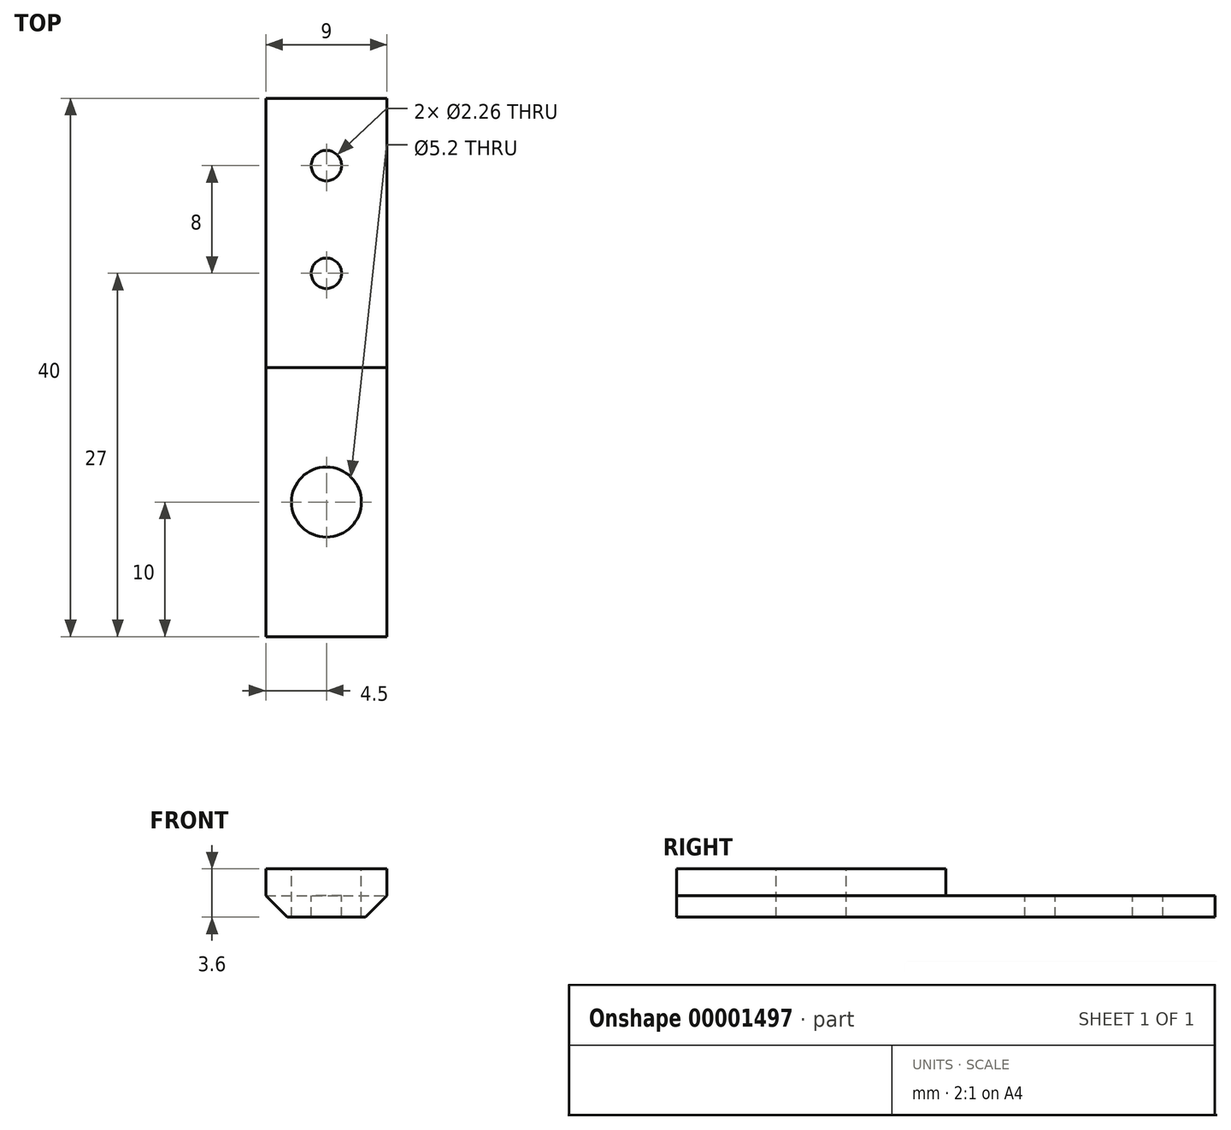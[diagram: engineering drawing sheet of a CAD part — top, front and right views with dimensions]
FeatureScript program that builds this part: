
annotation { "Feature Type Name" : "Feature", "Feature Type Description" : "" }
export const myFeature = defineFeature(function(context is Context, id is Id, definition is map)
    precondition{}
    {
        {
            var Q0;
            Q0=qCreatedBy(makeId("Front.planeOp"),FACE);
            var sketch = newSketch(context, id + "F0", { "sketchPlane" : qUnion([Q0])});
            skLineSegment(sketch, "E0", {"start": v(-4.5, 0) * mm, "end": v(4.5, 0) * mm});
            skLineSegment(sketch, "E1", {"start": v(4.5, 0) * mm, "end": v(2.9, -1.6) * mm});
            skLineSegment(sketch, "E2", {"start": v(2.9, -1.6) * mm, "end": v(-2.9, -1.6) * mm});
            skLineSegment(sketch, "E3", {"start": v(-2.9, -1.6) * mm, "end": v(-4.5, 0) * mm});
            skPoint(sketch, "E4", {"position": v(0, 0) * mm});
            skSolve(sketch);
        }
        {
            var Q0;
            Q0=makeQuery(id+"F0.imprint","IMPRINT",FACE,{"disambiguationData":[TD([[makeQuery(id+"F0.imprint","IMPRINT",EDGE,{"derivedFrom":sQuery(id+"F0.wireOp",EDGE,"E0")}),-1.0]])]});
            extrude(context, id + "F1", {"entities" : qUnion([Q0]), "depth" : 40 * mm});
        }
        {
            var Q0;
            Q0=makeQuery(id+"F1.opExtrude","SWEPT_FACE",FACE,{"disambiguationData":[OSD([sQuery(id+"F0.wireOp",EDGE,"E0")])]});
            var sketch = newSketch(context, id + "F2", { "sketchPlane" : qUnion([Q0])});
            skLineSegment(sketch, "E5.bottom", {"start": v(-4.5, -40) * mm, "end": v(4.5, -40) * mm});
            skLineSegment(sketch, "E5.top", {"start": v(-4.5, -20) * mm, "end": v(4.5, -20) * mm});
            skLineSegment(sketch, "E5.left", {"start": v(-4.5, -40) * mm, "end": v(-4.5, -20) * mm});
            skLineSegment(sketch, "E5.right", {"start": v(4.5, -40) * mm, "end": v(4.5, -20) * mm});
            skSolve(sketch);
        }
        {
            var Q0;
            Q0=makeQuery(id+"F2.imprint","IMPRINT",FACE,{"disambiguationData":[TD([[makeQuery(id+"F2.imprint","IMPRINT",EDGE,{"derivedFrom":sQuery(id+"F2.wireOp",EDGE,"E5.bottom")}),1.0]])]});
            extrude(context, id + "F3", {"entities" : qUnion([Q0]), "operationType" : NewBodyOperationType.ADD, "depth" : 2 * mm});
        }
        {
            var Q0;
            Q0=makeQuery(id+"F3.opExtrude","CAP_FACE",FACE,{"disambiguationData":[OSD([sQuery(id+"F2.wireOp",EDGE,"E5.bottom"),sQuery(id+"F2.wireOp",EDGE,"E5.top"),sQuery(id+"F2.wireOp",EDGE,"E5.left"),sQuery(id+"F2.wireOp",EDGE,"E5.right")])],"isStart":false});
            var sketch = newSketch(context, id + "F4", { "sketchPlane" : qUnion([Q0])});
            skCircle(sketch, "E6", {"center": v(0, -30) * mm, "radius": 2.6 * mm});
            skPoint(sketch, "E7", {"position": v(4.5, -30) * mm});
            skSolve(sketch);
        }
        {
            var Q0;
            Q0=makeQuery(id+"F4.imprint","IMPRINT",FACE,{"disambiguationData":[TD([[makeQuery(id+"F4.imprint","IMPRINT",EDGE,{"derivedFrom":sQuery(id+"F4.wireOp",EDGE,"E6")}),1.0]])]});
            extrude(context, id + "F5", {"entities" : qUnion([Q0]), "operationType" : NewBodyOperationType.REMOVE, "endBound" : BoundingType.THROUGH_ALL, "oppositeDirection" : true, "depth" : 25 * mm});
        }
        {
            var Q0;
            Q0=makeQuery(id+"F3.opExtrude","CAP_FACE",FACE,{"disambiguationData":[OSD([sQuery(id+"F2.wireOp",EDGE,"E5.bottom"),sQuery(id+"F2.wireOp",EDGE,"E5.top"),sQuery(id+"F2.wireOp",EDGE,"E5.left"),sQuery(id+"F2.wireOp",EDGE,"E5.right")])],"isStart":false});
            var sketch = newSketch(context, id + "F6", { "sketchPlane" : qUnion([Q0])});
            skCircle(sketch, "E8", {"center": v(0, -30) * mm, "radius": 5 * mm});
            skSolve(sketch);
        }
        {
            var Q0;
            {var subQ0=makeQuery(id+"F6.imprint","IMPRINT",EDGE,{"derivedFrom":makeQuery(id+"F5.boolean.opBoolean","COPY",EDGE,{"derivedFrom":makeQuery(id+"F5.opExtrude","CAP_EDGE",EDGE,{"disambiguationData":[OSD([sQuery(id+"F4.wireOp",EDGE,"E6")])],"isStart":true})})});var subQ1=makeQuery(id+"F3.opExtrude","CAP_EDGE",EDGE,{"disambiguationData":[OSD([sQuery(id+"F2.wireOp",EDGE,"E5.left")])],"isStart":false});var subQ2=sQuery(id+"F6.wireOp",EDGE,"E8");var subQ4=makeQuery(id+"F6.imprint","INTERSECT",VERTEX,{"disambiguationData":[OD(0.0)],"derivedFrom":[subQ1,subQ2]});var subQ6=makeQuery(id+"F3.opExtrude","CAP_EDGE",EDGE,{"disambiguationData":[OSD([sQuery(id+"F2.wireOp",EDGE,"E5.right")])],"isStart":false});var subQ8=makeQuery(id+"F6.imprint","INTERSECT",VERTEX,{"disambiguationData":[OD(0.0)],"derivedFrom":[subQ6,subQ2]});Q0=qUnion([makeQuery(id+"F6.imprint","IMPRINT",FACE,{"disambiguationData":[TD([[subQ0,1.0]])]}),makeQuery(id+"F6.imprint","IMPRINT",FACE,{"disambiguationData":[TD([[makeQuery(id+"F6.imprint","IMPRINT",EDGE,{"disambiguationData":[TD([[subQ4,-1.0]])],"derivedFrom":subQ2}),1.0]])]}),makeQuery(id+"F6.imprint","IMPRINT",FACE,{"disambiguationData":[TD([[makeQuery(id+"F6.imprint","IMPRINT",EDGE,{"disambiguationData":[TD([[subQ8,1.0]])],"derivedFrom":subQ2}),1.0]])]}),makeQuery(id+"F6.imprint","IMPRINT",FACE,{"disambiguationData":[TD([[subQ0,-1.0]])]})]);}
            extrude(context, id + "F7", {"entities" : qUnion([Q0]), "operationType" : NewBodyOperationType.REMOVE, "oppositeDirection" : true, "depth" : 1.6 * mm});
        }
        {
            var Q0;
            Q0=makeQuery(id+"F1.opExtrude","SWEPT_FACE",FACE,{"disambiguationData":[OSD([sQuery(id+"F0.wireOp",EDGE,"E0")])]});
            var sketch = newSketch(context, id + "F8", { "sketchPlane" : qUnion([Q0])});
            skCircle(sketch, "E9", {"center": v(0, -5) * mm, "radius": 1.13 * mm});
            skCircle(sketch, "E10", {"center": v(0, -13) * mm, "radius": 1.13 * mm});
            skSolve(sketch);
        }
        {
            var Q0;
            {Q0=qUnion([makeQuery(id+"F8.imprint","IMPRINT",FACE,{"disambiguationData":[TD([[makeQuery(id+"F8.imprint","IMPRINT",EDGE,{"derivedFrom":sQuery(id+"F8.wireOp",EDGE,"E9")}),1.0]])]}),makeQuery(id+"F8.imprint","IMPRINT",FACE,{"disambiguationData":[TD([[makeQuery(id+"F8.imprint","IMPRINT",EDGE,{"derivedFrom":sQuery(id+"F8.wireOp",EDGE,"E10")}),1.0]])]})]);}
            extrude(context, id + "F9", {"entities" : qUnion([Q0]), "operationType" : NewBodyOperationType.REMOVE, "endBound" : BoundingType.THROUGH_ALL, "oppositeDirection" : true, "depth" : 25 * mm});
        }
    });
